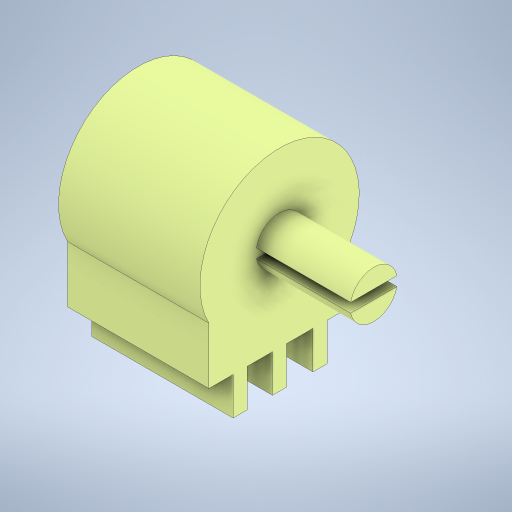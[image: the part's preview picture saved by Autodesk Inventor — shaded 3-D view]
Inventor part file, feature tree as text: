
AUTODESK INVENTOR PART (.ipt)
format: ipt  version: 2024 (Build 280153000, 153)  size: 292,864 bytes
history: native  units: mm
features: extrude x3, sketch x3, other x1
ambient origin geometry x8: Origin, YZ Plane, XZ Plane, XY Plane, X Axis, Y Axis, Z Axis, Center Point
bodies: Body1 (feature_tree)
feature tree (7):
  other  "솔리드1"
  extrude  "돌출1"  Depth=16.9mm
  extrude  "돌출2"  Depth=15.0mm TaperAngle=0.0deg
  extrude  "돌출3"  Depth=5.0mm
  sketch  "스케치1"
  sketch  "스케치2"
  sketch  "스케치3"
